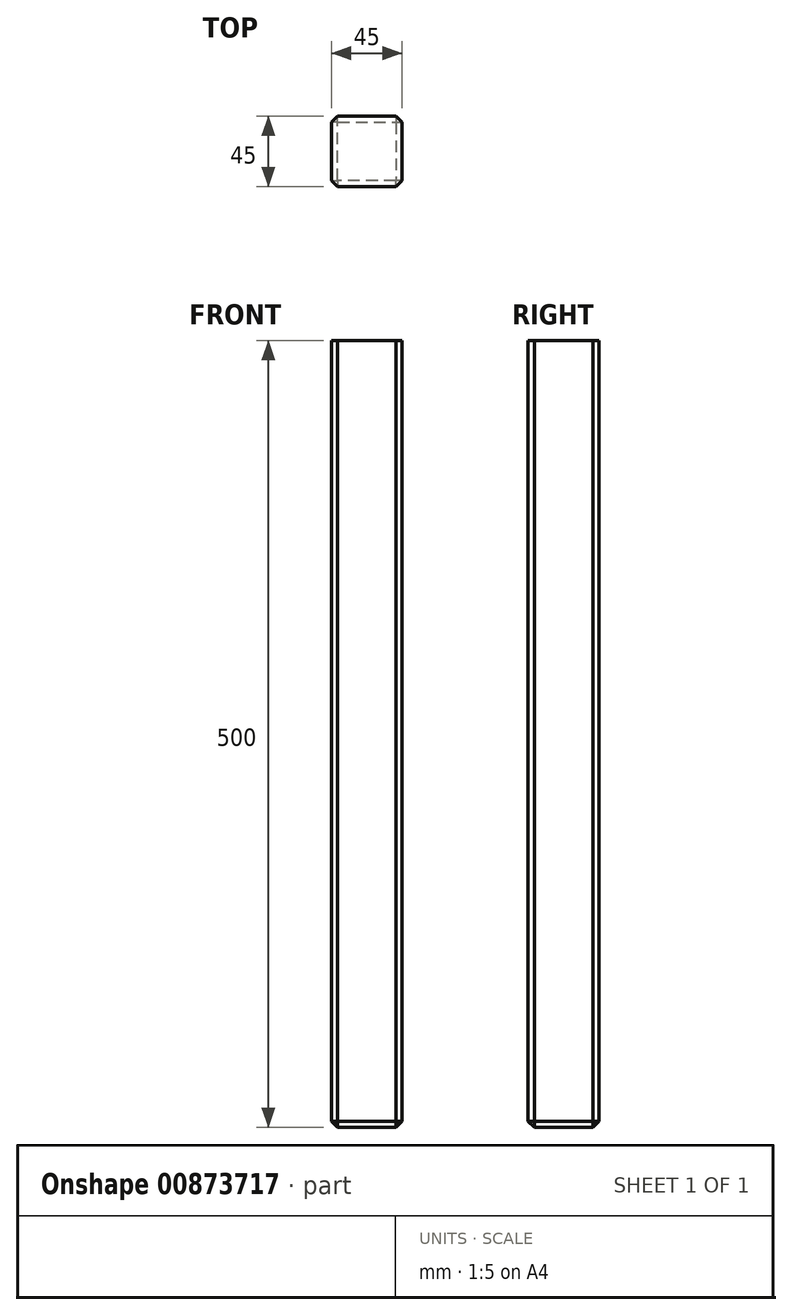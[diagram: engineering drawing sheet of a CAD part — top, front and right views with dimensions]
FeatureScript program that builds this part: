
annotation { "Feature Type Name" : "Feature", "Feature Type Description" : "" }
export const myFeature = defineFeature(function(context is Context, id is Id, definition is map)
    precondition{}
    {
        {
            var Q0;
            Q0=qCreatedBy(makeId("Front.planeOp"),FACE);
            var sketch = newSketch(context, id + "F0", { "sketchPlane" : qUnion([Q0])});
            skLineSegment(sketch, "E0.bottom", {"start": v(0, 0) * mm, "end": v(45, 0) * mm});
            skLineSegment(sketch, "E0.top", {"start": v(0, 500) * mm, "end": v(45, 500) * mm});
            skLineSegment(sketch, "E0.left", {"start": v(0, 0) * mm, "end": v(0, 500) * mm});
            skLineSegment(sketch, "E0.right", {"start": v(45, 0) * mm, "end": v(45, 500) * mm});
            skSolve(sketch);
        }
        {
            var Q0;
            Q0 = qSketchRegion(id + "F0", true);
            extrude(context, id + "F1", {"entities" : qUnion([Q0]), "depth" : 45 * mm, "offsetDistance" : 25 * mm});
        }
        {
            var Q0;
            Q0=makeQuery(id+"F1.opExtrude","CAP_EDGE",EDGE,{"disambiguationData":[OSD([sQuery(id+"F0.wireOp",EDGE,"E0.left")])],"isStart":false});
            var Q1;
            Q1=makeQuery(id+"F1.opExtrude","CAP_EDGE",EDGE,{"disambiguationData":[OSD([sQuery(id+"F0.wireOp",EDGE,"E0.right")])],"isStart":false});
            var Q2;
            Q2=makeQuery(id+"F1.opExtrude","CAP_EDGE",EDGE,{"disambiguationData":[OSD([sQuery(id+"F0.wireOp",EDGE,"E0.right")])],"isStart":true});
            var Q3;
            Q3=makeQuery(id+"F1.opExtrude","CAP_EDGE",EDGE,{"disambiguationData":[OSD([sQuery(id+"F0.wireOp",EDGE,"E0.left")])],"isStart":true});
            var Q4;
            Q4=makeQuery(id+"F1.opExtrude","CAP_EDGE",EDGE,{"disambiguationData":[OSD([sQuery(id+"F0.wireOp",EDGE,"E0.bottom")])],"isStart":true});
            var Q5;
            Q5=makeQuery(id+"F1.opExtrude","SWEPT_EDGE",EDGE,{"disambiguationData":[OSD([sQuery(id+"F0.wireOp",EDGE,"E0.bottom"),sQuery(id+"F0.wireOp",EDGE,"E0.right")])]});
            var Q6;
            Q6=makeQuery(id+"F1.opExtrude","SWEPT_EDGE",EDGE,{"disambiguationData":[OSD([sQuery(id+"F0.wireOp",EDGE,"E0.bottom"),sQuery(id+"F0.wireOp",EDGE,"E0.left")])]});
            var Q7;
            Q7=makeQuery(id+"F1.opExtrude","CAP_EDGE",EDGE,{"disambiguationData":[OSD([sQuery(id+"F0.wireOp",EDGE,"E0.bottom")])],"isStart":false});
            chamfer(context, id + "F2", {"entities" : qUnion([Q0, Q1, Q2, Q3, Q4, Q5, Q6, Q7]), "width" : 4 * mm, "tangentPropagation" : true});
        }
    });
